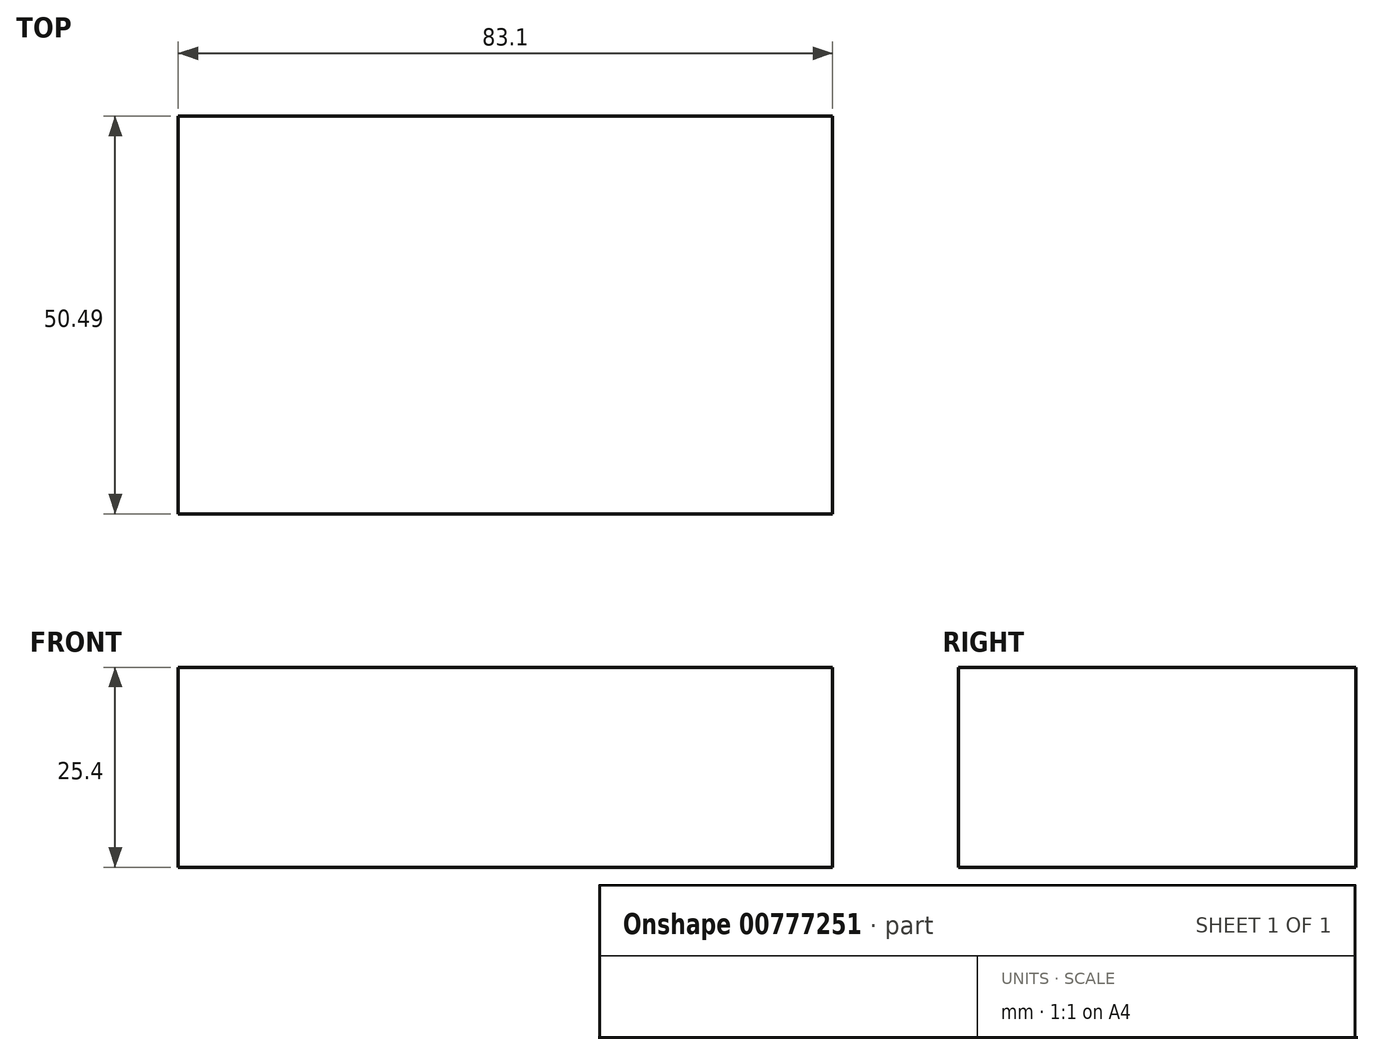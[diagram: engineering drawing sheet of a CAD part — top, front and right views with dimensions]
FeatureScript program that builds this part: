
annotation { "Feature Type Name" : "Feature", "Feature Type Description" : "" }
export const myFeature = defineFeature(function(context is Context, id is Id, definition is map)
    precondition{}
    {
        {
            var Q0;
            Q0=qCreatedBy(makeId("Top.planeOp"),FACE);
            var sketch = newSketch(context, id + "F0", { "sketchPlane" : qUnion([Q0])});
            skLineSegment(sketch, "E0.bottom", {"start": v(0, 0) * mm, "end": v(83.1, 0) * mm});
            skLineSegment(sketch, "E0.top", {"start": v(0, 25.09) * mm, "end": v(83.1, 25.09) * mm});
            skLineSegment(sketch, "E0.left", {"start": v(0, 0) * mm, "end": v(0, 25.09) * mm});
            skLineSegment(sketch, "E0.right", {"start": v(83.1, 0) * mm, "end": v(83.1, 25.09) * mm});
            skSolve(sketch);
        }
        {
            var Q0;
            Q0=makeQuery(id+"F0.imprint","IMPRINT",FACE,{"disambiguationData":[TD([[makeQuery(id+"F0.imprint","IMPRINT",EDGE,{"derivedFrom":sQuery(id+"F0.wireOp",EDGE,"E0.bottom")}),1.0]])]});
            extrude(context, id + "F1", {"entities" : qUnion([Q0]), "depth" : 25.4 * mm, "offsetDistance" : 25.4 * mm});
        }
        {
            var Q0;
            Q0=makeQuery(id+"F1.opExtrude","SWEPT_FACE",FACE,{"disambiguationData":[OSD([sQuery(id+"F0.wireOp",EDGE,"E0.bottom")])]});
            extrude(context, id + "F2", {"entities" : qUnion([Q0]), "operationType" : NewBodyOperationType.ADD, "depth" : 25.4 * mm, "offsetDistance" : 25.4 * mm});
        }
    });
